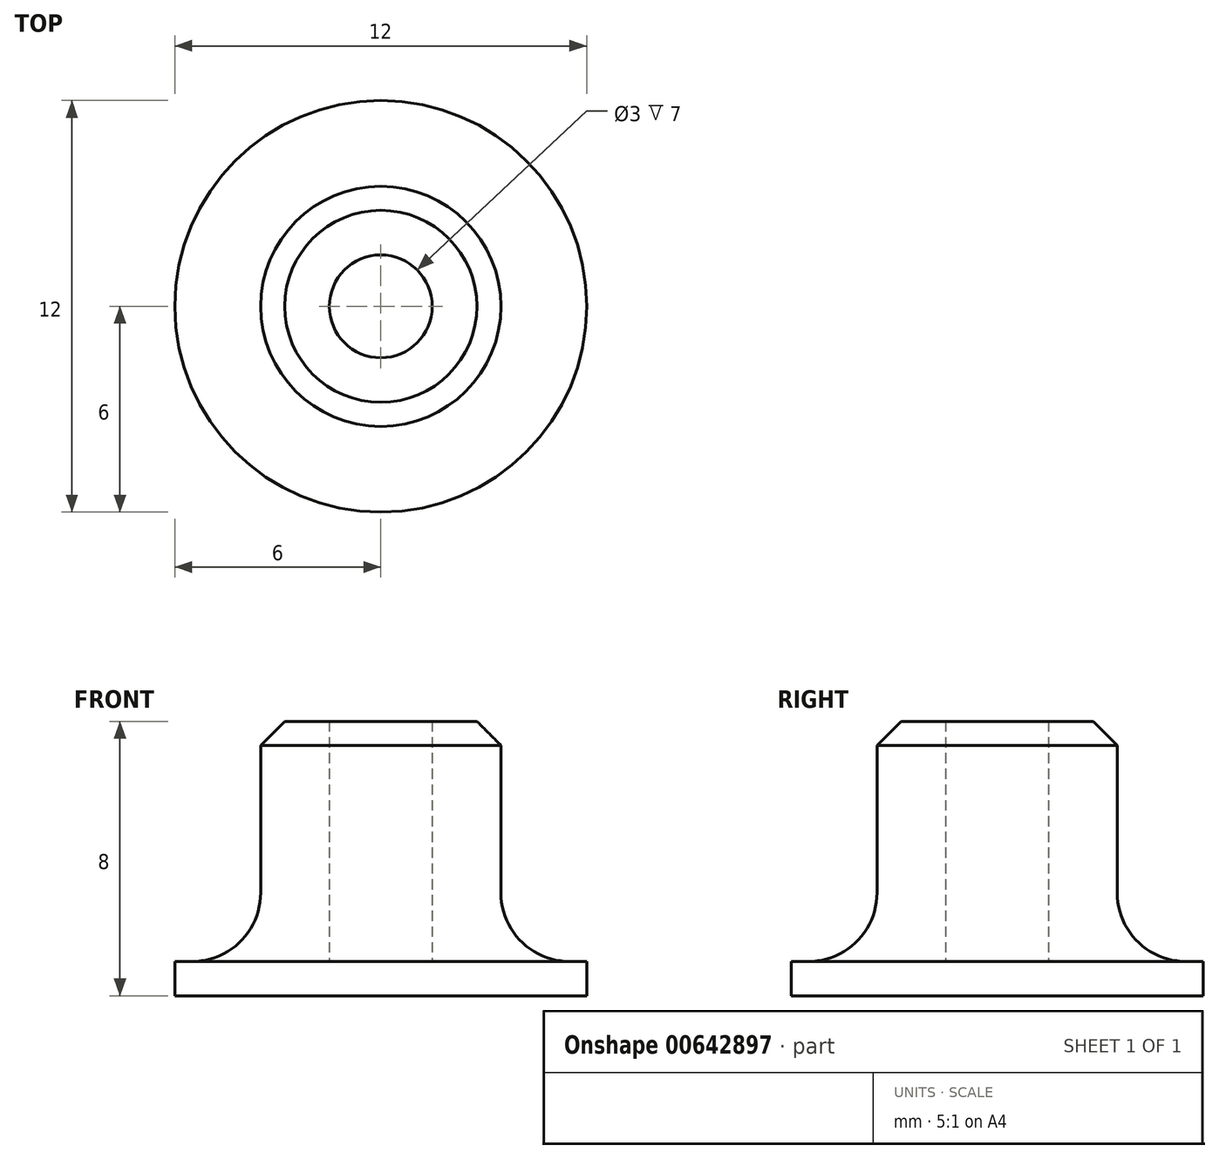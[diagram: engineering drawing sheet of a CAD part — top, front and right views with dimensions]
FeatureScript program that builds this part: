
annotation { "Feature Type Name" : "Feature", "Feature Type Description" : "" }
export const myFeature = defineFeature(function(context is Context, id is Id, definition is map)
    precondition{}
    {
        {
            var Q0;
            Q0=qCreatedBy(makeId("Top.planeOp"),FACE);
            var sketch = newSketch(context, id + "F0", { "sketchPlane" : qUnion([Q0])});
            skCircle(sketch, "E0", {"center": v(0, 0) * mm, "radius": 6 * mm});
            skCircle(sketch, "E1", {"center": v(0, 0) * mm, "radius": 3.5 * mm});
            skCircle(sketch, "E2", {"center": v(0, 0) * mm, "radius": 1.5 * mm});
            skSolve(sketch);
        }
        {
            var Q0;
            Q0=makeQuery(id+"F0.imprint","IMPRINT",FACE,{"disambiguationData":[TD([[makeQuery(id+"F0.imprint","IMPRINT",EDGE,{"derivedFrom":sQuery(id+"F0.wireOp",EDGE,"E0")}),1.0]])]});
            var Q1;
            Q1=makeQuery(id+"F0.imprint","IMPRINT",FACE,{"disambiguationData":[TD([[makeQuery(id+"F0.imprint","IMPRINT",EDGE,{"derivedFrom":sQuery(id+"F0.wireOp",EDGE,"E1")}),1.0]])]});
            var Q2;
            Q2=makeQuery(id+"F0.imprint","IMPRINT",FACE,{"disambiguationData":[TD([[makeQuery(id+"F0.imprint","IMPRINT",EDGE,{"derivedFrom":sQuery(id+"F0.wireOp",EDGE,"E2")}),1.0]])]});
            extrude(context, id + "F1", {"entities" : qUnion([Q0, Q1, Q2]), "depth" : 1 * mm, "offsetDistance" : 25 * mm});
        }
        {
            var Q0;
            Q0=makeQuery(id+"F0.imprint","IMPRINT",FACE,{"disambiguationData":[TD([[makeQuery(id+"F0.imprint","IMPRINT",EDGE,{"derivedFrom":sQuery(id+"F0.wireOp",EDGE,"E1")}),1.0]])]});
            extrude(context, id + "F2", {"entities" : qUnion([Q0]), "operationType" : NewBodyOperationType.ADD, "depth" : 8 * mm, "offsetDistance" : 25 * mm});
        }
        {
            var Q0;
            Q0=makeQuery(id+"F2.boolean.opBoolean","INTERSECT",EDGE,{"derivedFrom":[makeQuery(id+"F1.opExtrude","CAP_FACE",FACE,{"disambiguationData":[OSD([sQuery(id+"F0.wireOp",EDGE,"E0")])],"isStart":false}),makeQuery(id+"F2.opExtrude","SWEPT_FACE",FACE,{"disambiguationData":[OSD([sQuery(id+"F0.wireOp",EDGE,"E1")])]})]});
            fillet(context, id + "F3", {"entities" : qUnion([Q0]), "radius" : 2 * mm, "tangentPropagation" : true, "allowEdgeOverflow" : false});
        }
        {
            var Q0;
            Q0=makeQuery(id+"F2.opExtrude","CAP_EDGE",EDGE,{"disambiguationData":[OSD([sQuery(id+"F0.wireOp",EDGE,"E1")])],"isStart":false});
            chamfer(context, id + "F4", {"entities" : qUnion([Q0]), "width" : 0.7 * mm, "tangentPropagation" : true});
        }
    });
